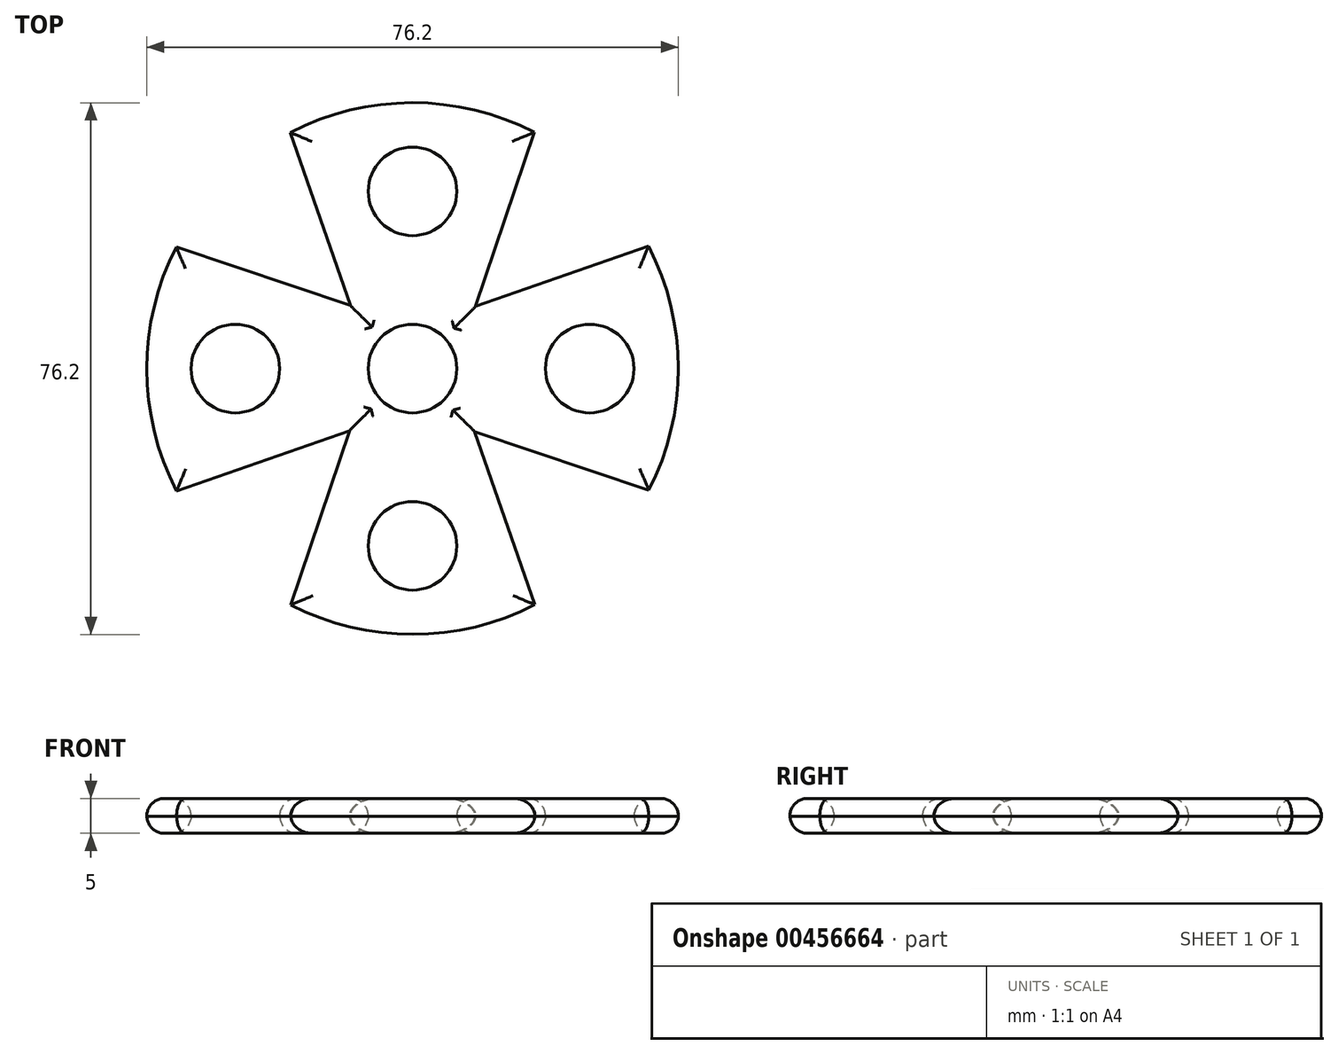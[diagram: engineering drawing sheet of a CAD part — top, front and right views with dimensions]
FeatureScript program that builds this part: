
annotation { "Feature Type Name" : "Feature", "Feature Type Description" : "" }
export const myFeature = defineFeature(function(context is Context, id is Id, definition is map)
    precondition{}
    {
        {
            var Q0;
            Q0=qCreatedBy(makeId("Top.planeOp"),FACE);
            var sketch = newSketch(context, id + "F0", { "sketchPlane" : qUnion([Q0])});
            skCircle(sketch, "E0", {"center": v(0, 0) * mm, "radius": 38.1 * mm});
            skSolve(sketch);
        }
        {
            var Q0;
            Q0 = qSketchRegion(id + "F0", true);
            extrude(context, id + "F1", {"entities" : qUnion([Q0]), "depth" : 5 * mm, "offsetDistance" : 25.4 * mm});
        }
        {
            var Q0;
            Q0=qCreatedBy(makeId("Top.planeOp"),FACE);
            var sketch = newSketch(context, id + "F2", { "sketchPlane" : qUnion([Q0])});
            skCircle(sketch, "E1", {"center": v(0, 0) * mm, "radius": 6.35 * mm});
            skSolve(sketch);
        }
        {
            var Q0;
            Q0 = qSketchRegion(id + "F2", true);
            extrude(context, id + "F3", {"entities" : qUnion([Q0]), "operationType" : NewBodyOperationType.REMOVE, "depth" : 25.4 * mm, "offsetDistance" : 25.4 * mm});
        }
        {
            var Q0;
            Q0=qCreatedBy(makeId("Top.planeOp"),FACE);
            var sketch = newSketch(context, id + "F4", { "sketchPlane" : qUnion([Q0])});
            skCircle(sketch, "E2", {"center": v(0, 0) * mm, "radius": 12.7 * mm, "construction": true});
            skCircle(sketch, "E3", {"center": v(-25.4, 0) * mm, "radius": 6.35 * mm});
            skCircle(sketch, "E4.1.0", {"center": v(0, -25.4) * mm, "radius": 6.35 * mm});
            skCircle(sketch, "E4.2.0", {"center": v(25.4, 0) * mm, "radius": 6.35 * mm});
            skCircle(sketch, "E4.3.0", {"center": v(0, 25.4) * mm, "radius": 6.35 * mm});
            skLineSegment(sketch, "E5", {"start": v(-44.75, 21.1) * mm, "end": v(-8.91, 9.05) * mm});
            skLineSegment(sketch, "E6", {"start": v(-8.91, 9.05) * mm, "end": v(-17.77, 34.46) * mm});
            skLineSegment(sketch, "E7", {"start": v(-44.75, 21.1) * mm, "end": v(-17.77, 34.46) * mm});
            skLineSegment(sketch, "E8.1.0", {"start": v(-21.1, -44.75) * mm, "end": v(-34.46, -17.77) * mm});
            skLineSegment(sketch, "E8.1.1", {"start": v(-9.05, -8.91) * mm, "end": v(-34.46, -17.77) * mm});
            skLineSegment(sketch, "E8.1.2", {"start": v(-21.1, -44.75) * mm, "end": v(-9.05, -8.91) * mm});
            skLineSegment(sketch, "E8.2.0", {"start": v(44.75, -21.1) * mm, "end": v(17.77, -34.46) * mm});
            skLineSegment(sketch, "E8.2.1", {"start": v(8.91, -9.05) * mm, "end": v(17.77, -34.46) * mm});
            skLineSegment(sketch, "E8.2.2", {"start": v(44.75, -21.1) * mm, "end": v(8.91, -9.05) * mm});
            skLineSegment(sketch, "E8.3.0", {"start": v(21.1, 44.75) * mm, "end": v(34.46, 17.77) * mm});
            skLineSegment(sketch, "E8.3.1", {"start": v(9.05, 8.91) * mm, "end": v(34.46, 17.77) * mm});
            skLineSegment(sketch, "E8.3.2", {"start": v(21.1, 44.75) * mm, "end": v(9.05, 8.91) * mm});
            skSolve(sketch);
        }
        {
            var Q0;
            Q0 = qSketchRegion(id + "F4", true);
            extrude(context, id + "F5", {"entities" : qUnion([Q0]), "operationType" : NewBodyOperationType.REMOVE, "depth" : 25.4 * mm, "offsetDistance" : 25.4 * mm});
        }
        {
            var Q0;
            Q0=makeQuery(id+"F1.opExtrude","CAP_FACE",FACE,{"disambiguationData":[OSD([sQuery(id+"F0.wireOp",EDGE,"E0")])],"isStart":false});
            fillet(context, id + "F6", {"entities" : qUnion([Q0]), "radius" : 2.54 * mm, "tangentPropagation" : true, "allowEdgeOverflow" : false});
        }
        {
            var Q0;
            Q0=makeQuery(id+"F1.opExtrude","CAP_FACE",FACE,{"disambiguationData":[OSD([sQuery(id+"F0.wireOp",EDGE,"E0")])],"isStart":true});
            fillet(context, id + "F7", {"entities" : qUnion([Q0]), "radius" : 2.54 * mm, "tangentPropagation" : true, "allowEdgeOverflow" : false});
        }
    });
